# Revit family: PM1225551-Cepillero-Greta-Mateblack
name_source: partatom
category: Plumbing Fixtures
units: mm (PartAtom-declared; Revit-internal decimal feet)

## family parameters
Always vertical = Yes
Cut with Voids When Loaded = No
Host = Wall
OmniClass Number = 23.25.17.13
Part Type = Normal
Room Calculation Point = No
Round Connector Dimension = Use Diameter
Shared = No

## types (1)
- Cepillero Palma
    Alto = 68 mm
    Ancho = 66 mm  [stored 0.216535 ft]
    Creado por = BIMBAU
    Default Elevation = 0 mm  [stored 0 ft]
    Description = Accesorios que reflejan las últimas tendencias de diseño convirtiéndose así en el mejor complemento para su baño. Contando con un sistema de instalación oculto en material metálico cromado que facilitan su limpieza y mantienen el diseño estilizado.
    Dimensiones generales del producto = 75 x 220 x 680 mm.
    Fecha de creación = 04/05/2021
    Garantía = 3 años - 3 años Cromado.
    Manufacturer = Corona.
    Material = Corona_mate_black
    Material 2 = Corona_Plastico_Blanco
    Model = PM1055551_Cepillero Palma.
    Peso Neto aprox = 1090 gr. (2.4030 lb.)
    Profundidad = 119 mm  [stored 0.39042 ft]
    Recubrimientos = Resistente a la corrosión, pelado y decoloración por agua. Recubrimiento no tóxico. Producto para uso doméstico.

note: [stored X ft] marks values corroborated as IEEE doubles in the binary element streams (Revit-internal decimal feet)

## geometry (parser evidence)
native form markers: Sweep x5
no freeform markers — native parametric forms only
